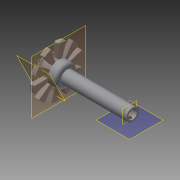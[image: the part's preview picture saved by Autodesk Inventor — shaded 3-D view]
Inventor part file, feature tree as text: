
AUTODESK INVENTOR PART (.ipt)
format: ipt  version: 2015 (Build 190159000, 159)  size: 227,328 bytes
history: native  units: mm
features: sketch x15, extrude x10, plane x5, pattern_circular x2, sweep x2, fillet x1
ambient origin geometry x8: Origin, YZ Plane, XZ Plane, XY Plane, X Axis, Y Axis, Z Axis, Center Point
bodies: Solid1 (feature_tree)
feature tree (35):
  extrude  "Extrusion1"  Depth=3.141593mm
  pattern_circular  "Circular Pattern1"  Count=10 Angle=360.0deg
  plane  "Work Plane1"
  extrude  "Extrusion2"  Depth=14.0mm
  extrude  "Extrusion3"  Depth=3.0mm TaperAngle=0.0deg
  extrude  "Extrusion4"  Depth=8.2mm
  extrude  "Extrusion5"  Depth=1.85mm
  extrude  "Extrusion6"  Depth=1.0mm TaperAngle=0.0deg
  extrude  "Extrusion7"  Depth=5.8mm
  fillet  "Fillet1"  Radius=40.0mm
  extrude  "Extrusion8"  [1 undecoded]
  extrude  "Extrusion9"  TaperAngle=0.0deg  [1 undecoded]
  plane  "Work Plane2"
  sketch  "Sketch10"  dims[d31=2.5mm d32=0.0mm d33=0.0mm]
  plane  "Work Plane3"
  sweep  "Sweep1"
  plane  "Work Plane4"
  sketch  "Sketch12"  dims[d36=3.0mm d37=0.0mm d38=0.0mm]
  plane  "Work Plane5"
  sweep  "Sweep2"
  sketch  "Sketch14"
  extrude  "Extrusion10"  Depth=5.0mm TaperAngle=0.0deg
  pattern_circular  "Circular Pattern2"  Count=3 Angle=360.0deg
  sketch  "Sketch1"  dims[d0=16.0mm d1=3.141593mm]
  sketch  "Sketch2"  dims[d3=3.0mm d4=0.0mm d5=100.0mm d6=360.0deg]
  sketch  "Sketch3"  dims[d8=3.0mm d9=14.0mm]
  sketch  "Sketch4"  dims[d10=4.5mm d11=0.0mm d12=3.0mm d13=0.0mm]
  sketch  "Sketch5"  dims[d14=4.5mm d15=0.0mm d16=8.2mm]
  sketch  "Sketch6"  dims[d17=40.0mm d18=0.0mm d19=1.85mm]
  sketch  "Sketch7"  dims[d20=9.0mm d21=0.0mm d22=1.0mm d23=0.0mm]
  sketch  "Sketch8"  dims[d24=2.0mm d25=5.8mm d26=40.0mm d27=0.0mm]
  sketch  "Sketch9"  dims[d28=4.0mm d29=0.0mm d30=-2.0mm]
  sketch  "Sketch11"  dims[d34=-2.0mm d35=2.0mm]
  sketch  "Sketch13"  dims[d39=1.6mm d40=5.0mm d41=0.0mm d42=30.0mm d43=360.0deg]
  sketch  "Sketch15"
note: 2 required parameter values undecoded (feature->parameter linkage not recoverable at this tier; creation-order binding heuristic only, values carry confidence <= 0.55)
